# Revit family: Fireplace_Wood_HeatNGlo_Castlewood
name_source: partatom
category: Mechanical Equipment
revit_build: Autodesk Revit 2015 (Build: 20140323_1530(x64)
units: mm (PartAtom-declared; Revit-internal decimal feet)

## types (3) — shared parameters
Assembly Code = D3020
Construction Details = http://www.arcat.com
Default Elevation = 0' - 0"
Efficiency Ratings = as Specified
Fixture Finish = Metal - HeatNGlo - Metallic Black
Fuel Consumption = as Specified
HVAC_BTU Input = 0.0 Btu/h
HVAC_BTU Output = 0.0 Btu/h
Heating Capacity = as Specified
Keynote = 10305
Manufacturer = Heat & Glo
Manufacturer Website = http://www.heatnglo.com
Model = Castlewood
Opening Height = 3' - 2"
Opening Width = 3' - 5 7/8"
Product Data = http://www.arcat.com
Revision = R2_2014-11
Sales Information = http://www.heatnglo.com
Send Message = http://www.arcat.com
Specification = http://www.arcat.com
Standards Conformance = as Specified
URL = http://www.heatnglo.com
Unit Depth = 2' - 3 1/2"
Unit Height = 6' - 2 1/8"
Unit Weight = 340
Unit Width = 4' - 4 7/8"
zero-valued in all types: Expected Lifespan (Years), Maintenance Schedule (Months), Warranty Duration (Years)

## per-type parameters (varying)
| type | Description | Fuel Type |
| 42x38 Viewing Area Gas Burning LP | Heat & Glo Gas Burning Outdoor Fireplace - Castlewood as Specified | NG |
| 42x38 Viewing Area Gas Burning NG | Heat & Glo Gas Burning Outdoor Fireplace - Castlewood as Specified | NG |
| 42x38 Viewing Area Wood Burning | Heat & Glo Woodburning Outdoor Fireplace - Castlewood as Specified | Wood |

## geometry (parser evidence)
native form markers: Blend x10, Sweep x3
no freeform markers — native parametric forms only
